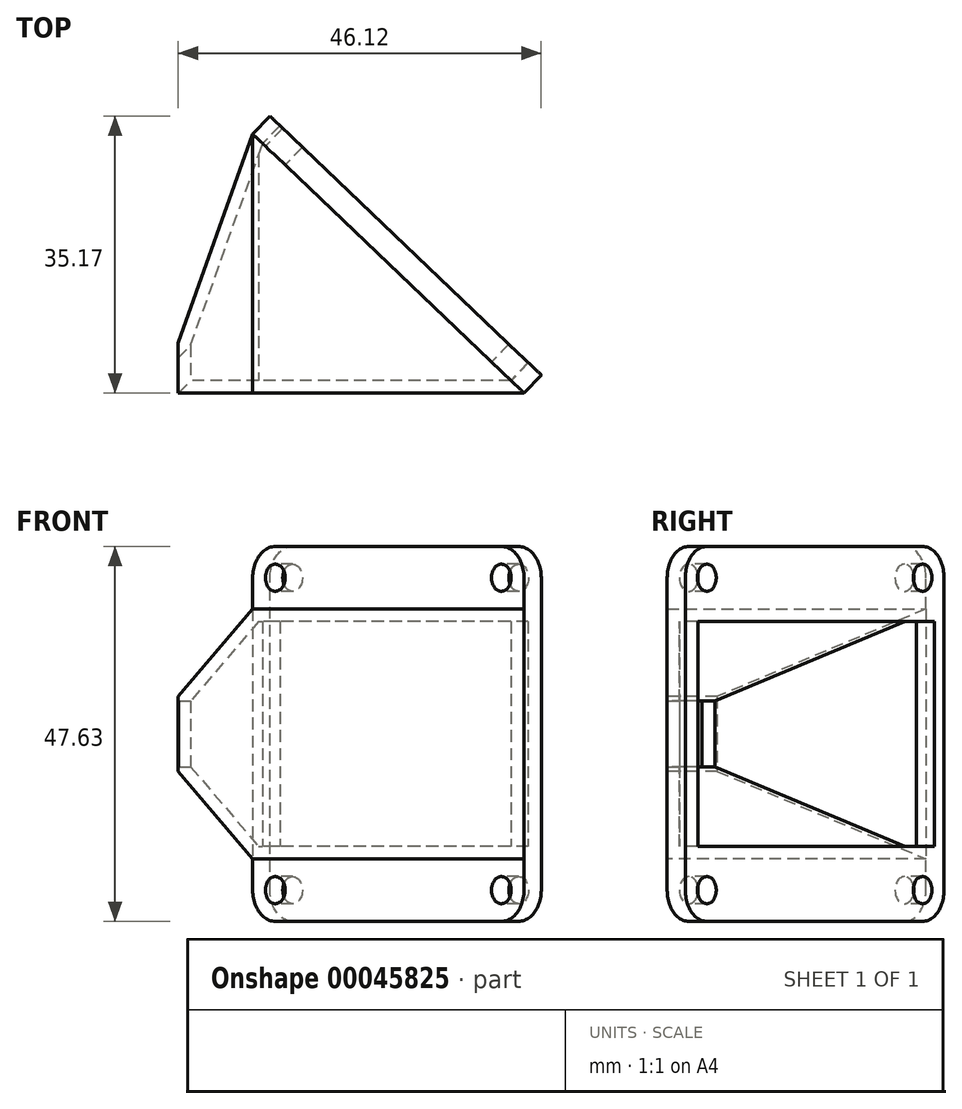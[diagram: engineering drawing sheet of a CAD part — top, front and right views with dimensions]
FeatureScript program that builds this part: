
annotation { "Feature Type Name" : "Feature", "Feature Type Description" : "" }
export const myFeature = defineFeature(function(context is Context, id is Id, definition is map)
    precondition{}
    {
        {
            var Q0;
            Q0=qCreatedBy(makeId("Top.planeOp"),FACE);
            var sketch = newSketch(context, id + "F0", { "sketchPlane" : qUnion([Q0])});
            skLineSegment(sketch, "E0", {"start": v(0, 0) * mm, "end": v(-34.46, 32.88) * mm});
            skLineSegment(sketch, "E1", {"start": v(0, 0) * mm, "end": v(-43.93, 0) * mm});
            skLineSegment(sketch, "E2", {"start": v(-34.46, 32.88) * mm, "end": v(-43.93, 6.35) * mm});
            skLineSegment(sketch, "E3", {"start": v(-43.93, 0) * mm, "end": v(-43.93, 6.35) * mm});
            skSolve(sketch);
        }
        {
            var Q0;
            Q0=qSketchRegion(id+"F0",true);
            extrude(context, id + "F1", {"entities" : qUnion([Q0]), "depth" : 31.75 * mm});
        }
        {
            var Q0;
            Q0=makeQuery(id+"F1.opExtrude","SWEPT_FACE",FACE,{"disambiguationData":[OSD([sQuery(id+"F0.wireOp",EDGE,"E1")])]});
            var sketch = newSketch(context, id + "F2", { "sketchPlane" : qUnion([Q0])});
            skLineSegment(sketch, "E4.bottom", {"start": v(-43.93, 11.11) * mm, "end": v(-34.46, 11.11) * mm, "construction": true});
            skLineSegment(sketch, "E4.top", {"start": v(-43.93, 0) * mm, "end": v(-34.46, 0) * mm});
            skLineSegment(sketch, "E4.left", {"start": v(-43.93, 11.11) * mm, "end": v(-43.93, 0) * mm});
            skLineSegment(sketch, "E4.right", {"start": v(-34.46, 11.11) * mm, "end": v(-34.46, 0) * mm, "construction": true});
            skLineSegment(sketch, "E5.bottom", {"start": v(-43.93, 31.75) * mm, "end": v(-34.46, 31.75) * mm});
            skLineSegment(sketch, "E5.top", {"start": v(-43.93, 20.64) * mm, "end": v(-34.46, 20.64) * mm, "construction": true});
            skLineSegment(sketch, "E5.left", {"start": v(-43.93, 31.75) * mm, "end": v(-43.93, 20.64) * mm});
            skLineSegment(sketch, "E5.right", {"start": v(-34.46, 31.75) * mm, "end": v(-34.46, 20.64) * mm, "construction": true});
            skLineSegment(sketch, "E6", {"start": v(-34.46, 0) * mm, "end": v(-43.93, 11.11) * mm});
            skLineSegment(sketch, "E7", {"start": v(-43.93, 20.64) * mm, "end": v(-34.46, 31.75) * mm});
            skSolve(sketch);
        }
        {
            var Q0;
            Q0=qSketchRegion(id+"F2",true);
            var Q1;
            Q1=makeQuery(id+"F1.opExtrude","SWEPT_FACE",FACE,{"disambiguationData":[OSD([sQuery(id+"F0.wireOp",EDGE,"E2")])]});
            extrude(context, id + "F3", {"entities" : qUnion([Q0]), "operationType" : NewBodyOperationType.REMOVE, "endBound" : BoundingType.UP_TO_SURFACE, "oppositeDirection" : true, "endBoundEntityFace" : qUnion([Q1]), "depth" : 25.4 * mm});
        }
        {
            var Q0;
            Q0=makeQuery(id+"F1.opExtrude","SWEPT_FACE",FACE,{"disambiguationData":[OSD([sQuery(id+"F0.wireOp",EDGE,"E0")])]});
            shell(context, id + "F4", {"entities" : qUnion([Q0]), "thickness" : 1.59 * mm});
        }
        {
            var Q0;
            Q0=makeQuery(id+"F1.opExtrude","SWEPT_FACE",FACE,{"disambiguationData":[OSD([sQuery(id+"F0.wireOp",EDGE,"E0")])]});
            var sketch = newSketch(context, id + "F5", { "sketchPlane" : qUnion([Q0])});
            skLineSegment(sketch, "E8.bottom", {"start": v(34.83, 11.7) * mm, "end": v(31.73, 11.7) * mm});
            skLineSegment(sketch, "E8.top", {"start": v(34.83, 20.05) * mm, "end": v(31.73, 20.05) * mm});
            skLineSegment(sketch, "E8.left", {"start": v(34.83, 11.7) * mm, "end": v(34.83, 20.05) * mm});
            skLineSegment(sketch, "E8.right", {"start": v(31.73, 11.7) * mm, "end": v(31.73, 20.05) * mm});
            skSolve(sketch);
        }
        {
            var Q0;
            Q0=qSketchRegion(id+"F5",true);
            var Q1;
            Q1=makeQuery(id+"F1.opExtrude","SWEPT_FACE",FACE,{"disambiguationData":[OSD([sQuery(id+"F0.wireOp",EDGE,"E3")])]});
            extrude(context, id + "F6", {"entities" : qUnion([Q0]), "operationType" : NewBodyOperationType.REMOVE, "endBound" : BoundingType.UP_TO_SURFACE, "oppositeDirection" : true, "endBoundEntityFace" : qUnion([Q1]), "depth" : 25.4 * mm});
        }
        {
            var Q0;
            Q0=makeQuery(id+"F1.opExtrude","SWEPT_FACE",FACE,{"disambiguationData":[OSD([sQuery(id+"F0.wireOp",EDGE,"E0")])]});
            var sketch = newSketch(context, id + "F7", { "sketchPlane" : qUnion([Q0])});
            skLineSegment(sketch, "E9.bottom", {"start": v(47.63, -7.94) * mm, "end": v(0, -7.94) * mm});
            skLineSegment(sketch, "E9.top", {"start": v(47.62, 39.69) * mm, "end": v(0, 39.69) * mm});
            skLineSegment(sketch, "E9.left", {"start": v(47.63, -7.94) * mm, "end": v(47.62, 39.69) * mm});
            skLineSegment(sketch, "E9.right", {"start": v(0, -7.94) * mm, "end": v(0, 39.69) * mm});
            skPoint(sketch, "E10", {"position": v(47.62, 15.88) * mm});
            skLineSegment(sketch, "E11.top", {"start": v(0, -3.97) * mm, "end": v(3.97, -3.97) * mm, "construction": true});
            skLineSegment(sketch, "E11.right", {"start": v(3.97, -7.94) * mm, "end": v(3.97, -3.97) * mm, "construction": true});
            skLineSegment(sketch, "E12.bottom", {"start": v(0, 35.72) * mm, "end": v(3.97, 35.72) * mm, "construction": true});
            skLineSegment(sketch, "E12.right", {"start": v(3.97, 35.72) * mm, "end": v(3.97, 39.69) * mm, "construction": true});
            skLineSegment(sketch, "E13", {"start": v(47.63, -3.97) * mm, "end": v(43.66, -3.97) * mm, "construction": true});
            skLineSegment(sketch, "E14", {"start": v(47.63, 35.72) * mm, "end": v(43.66, 35.72) * mm, "construction": true});
            skCircle(sketch, "E15", {"center": v(43.66, 35.72) * mm, "radius": 1.73 * mm});
            skCircle(sketch, "E16", {"center": v(3.97, 35.72) * mm, "radius": 1.73 * mm});
            skCircle(sketch, "E17", {"center": v(3.97, -3.97) * mm, "radius": 1.73 * mm});
            skCircle(sketch, "E18", {"center": v(43.66, -3.97) * mm, "radius": 1.73 * mm});
            skSolve(sketch);
        }
        {
            var Q0;
            {var subQ1=sQuery(id+"F7.wireOp",EDGE,"E9.bottom");Q0=makeQuery(id+"F7.imprint","IMPRINT",FACE,{"disambiguationData":[TD([[makeQuery(id+"F7.imprint","IMPRINT",EDGE,{"derivedFrom":subQ1}),-1.0]])]});}
            var Q1;
            {var subQ0=sQuery(id+"F7.wireOp",EDGE,"E9.top");Q1=makeQuery(id+"F7.imprint","IMPRINT",FACE,{"disambiguationData":[TD([[makeQuery(id+"F7.imprint","IMPRINT",EDGE,{"derivedFrom":subQ0}),1.0]])]});}
            var Q2;
            {var subQ0=sQuery(id+"F0.wireOp",EDGE,"E0");var subQ3=makeQuery(id+"F1.opExtrude","CAP_EDGE",EDGE,{"disambiguationData":[OSD([subQ0])],"isStart":true});Q2=makeQuery(id+"F7.imprint","IMPRINT",FACE,{"disambiguationData":[TD([[makeQuery(id+"F7.imprint","IMPRINT",EDGE,{"derivedFrom":subQ3}),1.0]])]});}
            extrude(context, id + "F8", {"entities" : qUnion([Q0, Q1, Q2]), "operationType" : NewBodyOperationType.ADD, "depth" : 3.17 * mm});
        }
        {
            var Q0;
            Q0=makeQuery(id+"F8.opExtrude","SWEPT_EDGE",EDGE,{"disambiguationData":[OSD([sQuery(id+"F7.wireOp",EDGE,"E9.bottom"),sQuery(id+"F7.wireOp",EDGE,"E9.left")])]});
            var Q1;
            Q1=makeQuery(id+"F8.opExtrude","SWEPT_EDGE",EDGE,{"disambiguationData":[OSD([sQuery(id+"F7.wireOp",EDGE,"E9.bottom"),sQuery(id+"F7.wireOp",EDGE,"E9.right")])]});
            var Q2;
            Q2=makeQuery(id+"F8.opExtrude","SWEPT_EDGE",EDGE,{"disambiguationData":[OSD([sQuery(id+"F7.wireOp",EDGE,"E9.top"),sQuery(id+"F7.wireOp",EDGE,"E9.left")])]});
            var Q3;
            Q3=makeQuery(id+"F8.opExtrude","SWEPT_EDGE",EDGE,{"disambiguationData":[OSD([sQuery(id+"F7.wireOp",EDGE,"E9.top"),sQuery(id+"F7.wireOp",EDGE,"E9.right")])]});
            fillet(context, id + "F9", {"entities" : qUnion([Q0, Q1, Q2, Q3]), "radius" : 3.97 * mm, "tangentPropagation" : true, "allowEdgeOverflow" : false});
        }
    });
